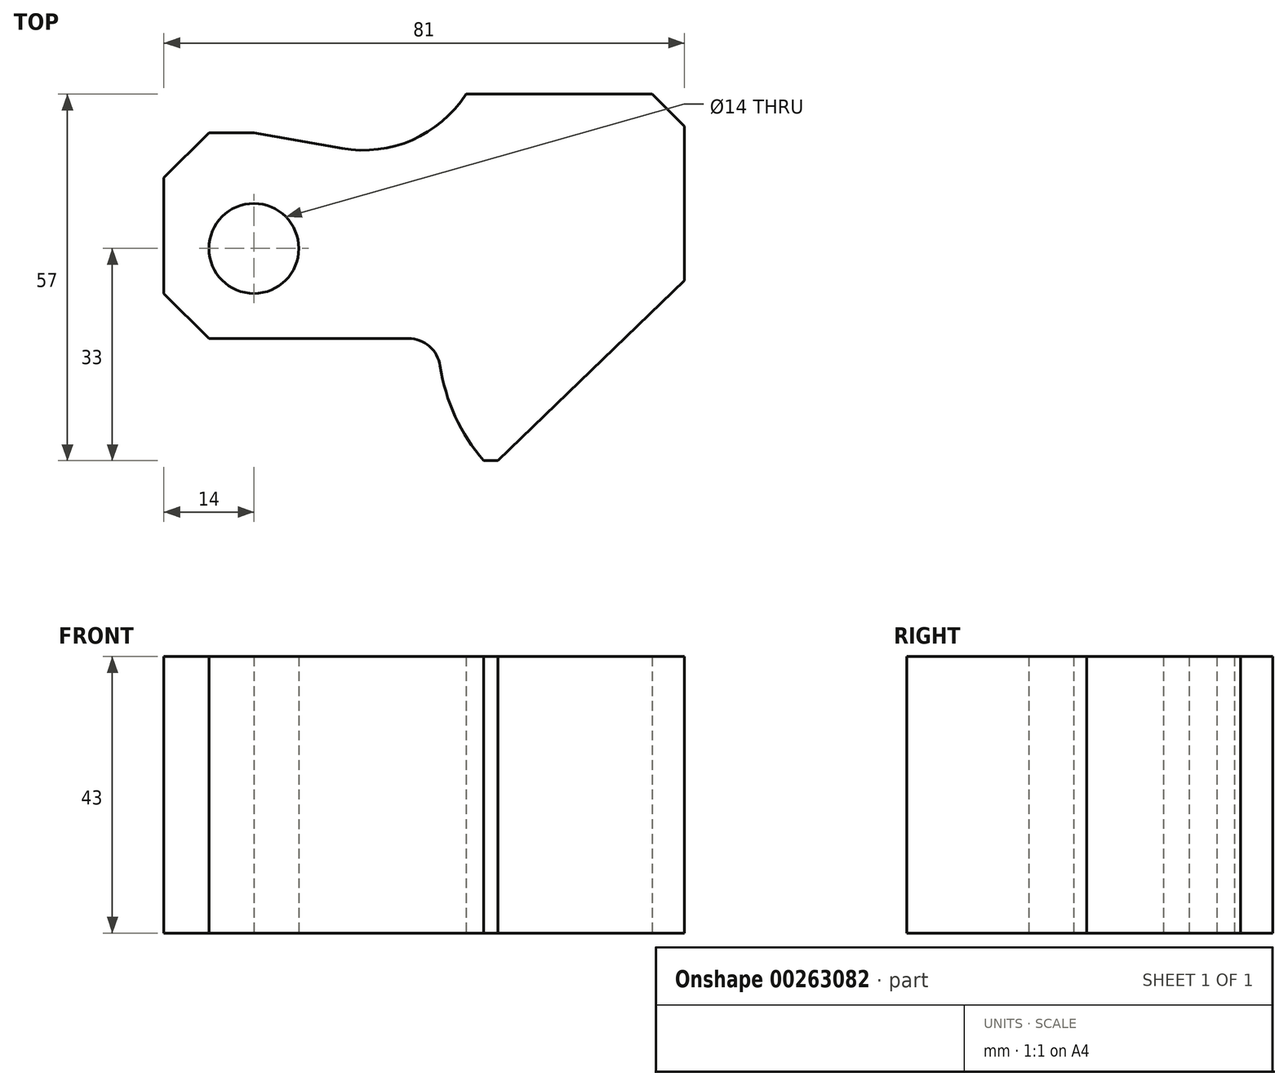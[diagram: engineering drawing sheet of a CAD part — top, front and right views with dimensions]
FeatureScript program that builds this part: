
annotation { "Feature Type Name" : "Feature", "Feature Type Description" : "" }
export const myFeature = defineFeature(function(context is Context, id is Id, definition is map)
    precondition{}
    {
        {
            var Q0;
            Q0=qCreatedBy(makeId("Top.planeOp"),FACE);
            var sketch = newSketch(context, id + "F0", { "sketchPlane" : qUnion([Q0])});
            skLineSegment(sketch, "E0", {"start": v(0, 0) * mm, "end": v(0, 18) * mm});
            skLineSegment(sketch, "E1", {"start": v(0, 18) * mm, "end": v(7, 25) * mm});
            skLineSegment(sketch, "E2", {"start": v(0, 0) * mm, "end": v(7, -7) * mm});
            skCircle(sketch, "E3", {"center": v(14, 7) * mm, "radius": 7 * mm});
            skLineSegment(sketch, "E4", {"start": v(7, 25) * mm, "end": v(14, 25) * mm});
            skLineSegment(sketch, "E5", {"start": v(47, 31) * mm, "end": v(76, 31) * mm});
            skLineSegment(sketch, "E6", {"start": v(76, 31) * mm, "end": v(81, 26) * mm});
            skLineSegment(sketch, "E7", {"start": v(81, 26) * mm, "end": v(81, 2) * mm});
            skLineSegment(sketch, "E8", {"start": v(81, 2) * mm, "end": v(52, -26) * mm});
            skLineSegment(sketch, "E9", {"start": v(14, 25) * mm, "end": v(27.73, 22.58) * mm});
            skArc(sketch, "E10", {"start": v(27.73, 22.58) * mm, "mid": v(38.64, 23.88) * mm, "end": v(47, 31) * mm});
            skArc(sketch, "E11", {"start": v(49.77, -26) * mm, "mid": v(45.33, -19.12) * mm, "end": v(43, -11.26) * mm});
            skLineSegment(sketch, "E12", {"start": v(7, -7) * mm, "end": v(38.05, -7) * mm});
            skArc(sketch, "E13", {"start": v(38.05, -7) * mm, "mid": v(41.31, -8.21) * mm, "end": v(43, -11.26) * mm});
            skLineSegment(sketch, "E14", {"start": v(49.77, -26) * mm, "end": v(52, -26) * mm});
            skSolve(sketch);
        }
        {
            var Q0;
            Q0 = qSketchRegion(id + "F0", true);
            extrude(context, id + "F1", {"entities" : qUnion([Q0]), "depth" : 43 * mm});
        }
    });
